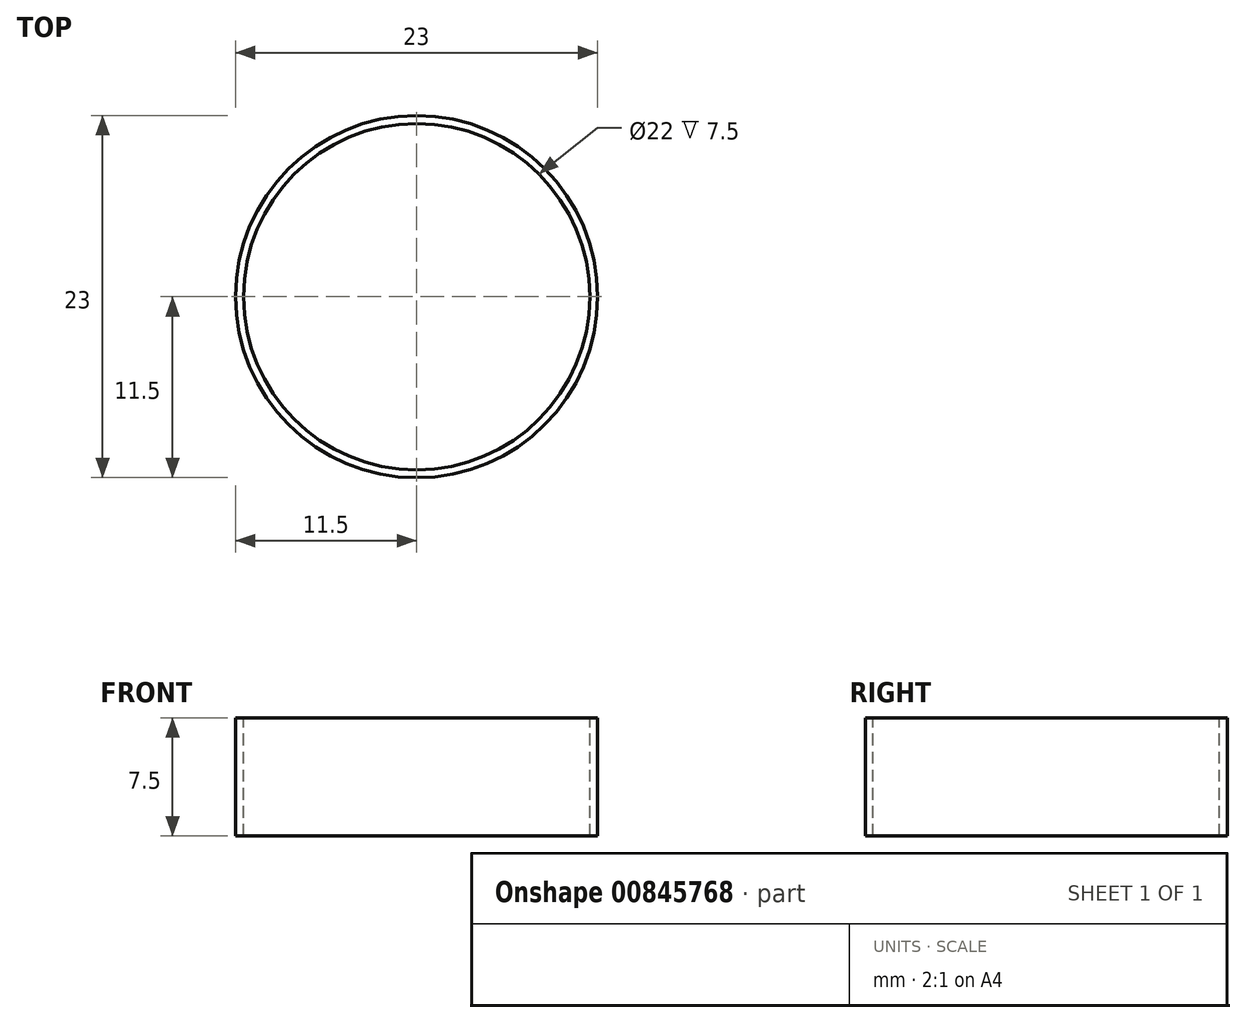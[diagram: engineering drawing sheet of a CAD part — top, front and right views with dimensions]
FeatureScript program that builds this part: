
annotation { "Feature Type Name" : "Feature", "Feature Type Description" : "" }
export const myFeature = defineFeature(function(context is Context, id is Id, definition is map)
    precondition{}
    {
        {
            var Q0;
            Q0=qCreatedBy(makeId("Top.planeOp"),FACE);
            var sketch = newSketch(context, id + "F0", { "sketchPlane" : qUnion([Q0])});
            skCircle(sketch, "E0", {"center": v(0, 0) * mm, "radius": 11 * mm});
            skCircle(sketch, "E1", {"center": v(0, 0) * mm, "radius": 11.5 * mm});
            skSolve(sketch);
        }
        {
            var Q0;
            Q0 = qSketchRegion(id + "F0", true);
            extrude(context, id + "F1", {"entities" : qUnion([Q0]), "oppositeDirection" : true, "depth" : 7.5 * mm, "offsetDistance" : 25 * mm});
        }
    });
